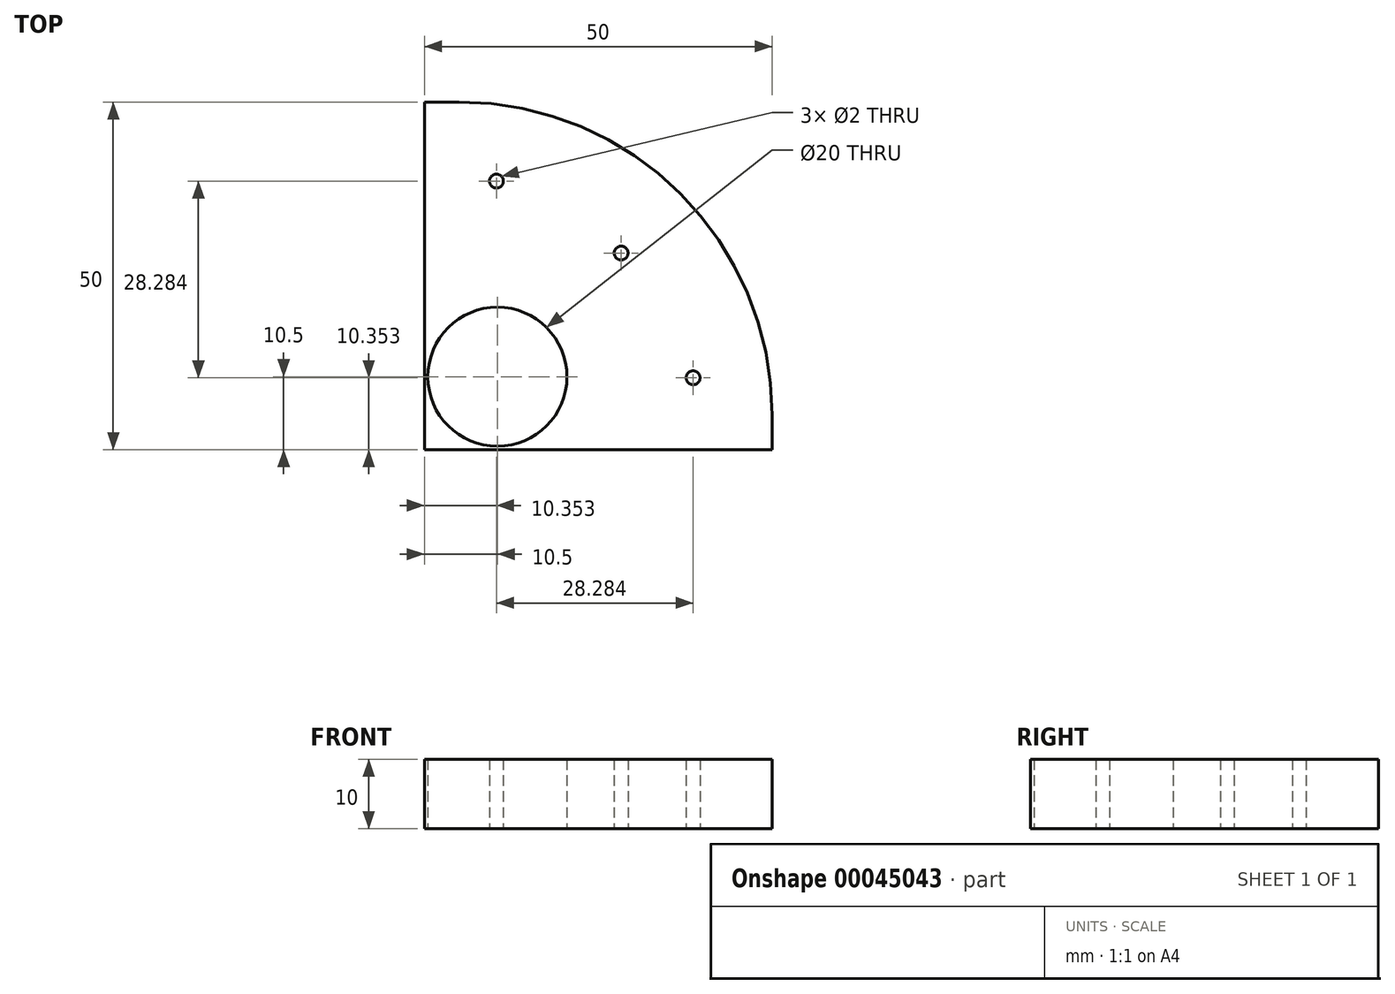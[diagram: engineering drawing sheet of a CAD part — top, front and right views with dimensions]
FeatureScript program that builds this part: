
annotation { "Feature Type Name" : "Feature", "Feature Type Description" : "" }
export const myFeature = defineFeature(function(context is Context, id is Id, definition is map)
    precondition{}
    {
        {
            var Q0;
            Q0=qCreatedBy(makeId("Top.planeOp"),FACE);
            var sketch = newSketch(context, id + "F0", { "sketchPlane" : qUnion([Q0])});
            skLineSegment(sketch, "E0.bottom", {"start": v(0, 0) * mm, "end": v(50, 0) * mm});
            skLineSegment(sketch, "E0.top", {"start": v(0, 50) * mm, "end": v(50, 50) * mm});
            skLineSegment(sketch, "E0.left", {"start": v(0, 0) * mm, "end": v(0, 50) * mm});
            skLineSegment(sketch, "E0.right", {"start": v(50, 0) * mm, "end": v(50, 50) * mm});
            skSolve(sketch);
        }
        {
            var Q0;
            Q0 = qSketchRegion(id + "F0", true);
            extrude(context, id + "F1", {"entities" : qUnion([Q0]), "depth" : 10 * mm});
        }
        {
            var Q0;
            Q0=makeQuery(id+"F1.opExtrude","CAP_FACE",FACE,{"disambiguationData":[OSD([sQuery(id+"F0.wireOp",EDGE,"E0.bottom"),sQuery(id+"F0.wireOp",EDGE,"E0.top"),sQuery(id+"F0.wireOp",EDGE,"E0.left"),sQuery(id+"F0.wireOp",EDGE,"E0.right")])],"isStart":true});
            var sketch = newSketch(context, id + "F2", { "sketchPlane" : qUnion([Q0])});
            skCircle(sketch, "E1", {"center": v(10.5, -10.5) * mm, "radius": 10 * mm});
            skSolve(sketch);
        }
        {
            var Q0;
            Q0=makeQuery(id+"F1.opExtrude","SWEPT_EDGE",EDGE,{"disambiguationData":[OSD([sQuery(id+"F0.wireOp",EDGE,"E0.top"),sQuery(id+"F0.wireOp",EDGE,"E0.right")])]});
            fillet(context, id + "F3", {"entities" : qUnion([Q0]), "radius" : 45 * mm, "tangentPropagation" : true, "allowEdgeOverflow" : false});
        }
        {
            var Q0;
            Q0=makeQuery(id+"F2.imprint","IMPRINT",FACE,{"disambiguationData":[TD([[makeQuery(id+"F2.imprint","IMPRINT",EDGE,{"derivedFrom":sQuery(id+"F2.wireOp",EDGE,"E1")}),-1.0]])]});
            var sketch = newSketch(context, id + "F4", { "sketchPlane" : qUnion([Q0])});
            skLineSegment(sketch, "E2", {"start": v(0, 0) * mm, "end": v(4.86, -18.14) * mm, "construction": true});
            skCircle(sketch, "E3", {"center": v(10.35, -38.64) * mm, "radius": 1 * mm});
            skCircle(sketch, "E4.1.0", {"center": v(28.28, -28.28) * mm, "radius": 1 * mm});
            skCircle(sketch, "E4.2.0", {"center": v(38.64, -10.35) * mm, "radius": 1 * mm});
            skPoint(sketch, "E4.center", {"position": v(0, 0) * mm});
            skLineSegment(sketch, "E4.anchor1", {"start": v(0, 0) * mm, "end": v(10.35, -38.64) * mm, "construction": true});
            skLineSegment(sketch, "E4.anchor2", {"start": v(0, 0) * mm, "end": v(38.64, -10.35) * mm, "construction": true});
            skSolve(sketch);
        }
        {
            var Q0;
            Q0 = qSketchRegion(id + "F2", true);
            extrude(context, id + "F5", {"entities" : qUnion([Q0]), "operationType" : NewBodyOperationType.REMOVE, "endBound" : BoundingType.THROUGH_ALL, "oppositeDirection" : true, "depth" : 25 * mm});
        }
        {
            var Q0;
            Q0 = qSketchRegion(id + "F4", true);
            extrude(context, id + "F6", {"entities" : qUnion([Q0]), "operationType" : NewBodyOperationType.REMOVE, "endBound" : BoundingType.THROUGH_ALL, "oppositeDirection" : true, "depth" : 25 * mm});
        }
    });
